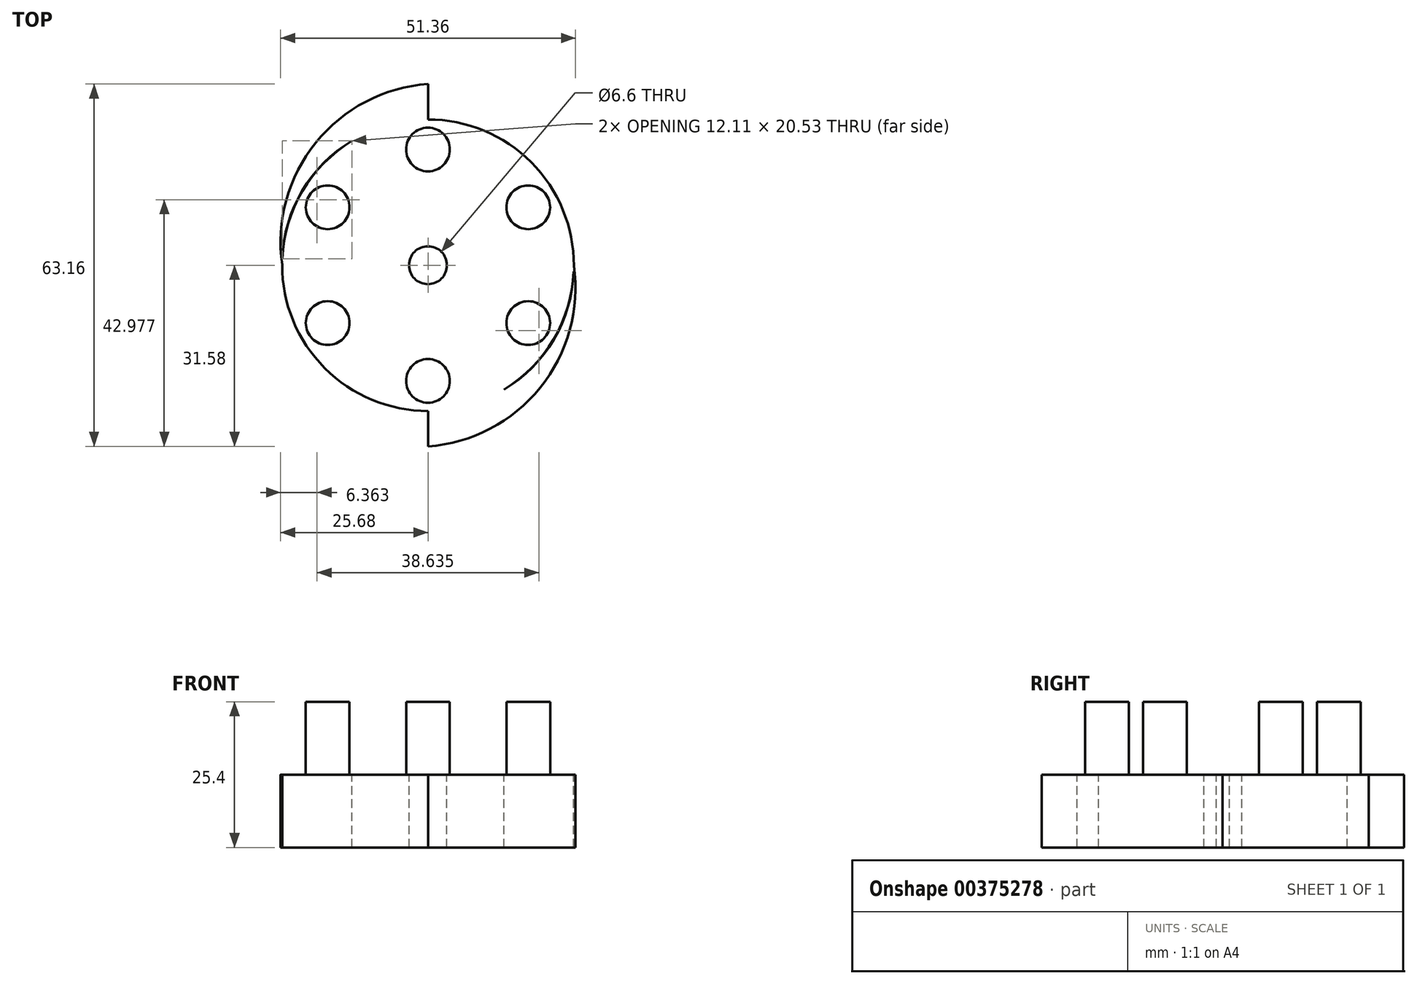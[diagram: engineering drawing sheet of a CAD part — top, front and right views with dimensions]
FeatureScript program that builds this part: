
annotation { "Feature Type Name" : "Feature", "Feature Type Description" : "" }
export const myFeature = defineFeature(function(context is Context, id is Id, definition is map)
    precondition{}
    {
        {
            var Q0;
            Q0=qCreatedBy(makeId("Top.planeOp"),FACE);
            var sketch = newSketch(context, id + "F0", { "sketchPlane" : qUnion([Q0])});
            skCircle(sketch, "E0", {"center": v(0, 0) * mm, "radius": 25.4 * mm});
            skSolve(sketch);
        }
        {
            var Q0;
            Q0 = qSketchRegion(id + "F0", true);
            extrude(context, id + "F1", {"entities" : qUnion([Q0]), "oppositeDirection" : true, "depth" : 12.7 * mm});
        }
        {
            var Q0;
            Q0=qCreatedBy(makeId("Top.planeOp"),FACE);
            var sketch = newSketch(context, id + "F2", { "sketchPlane" : qUnion([Q0])});
            skLineSegment(sketch, "E1", {"start": v(0, 25.2) * mm, "end": v(0, 31.58) * mm});
            skArc(sketch, "E2", {"start": v(0, 31.58) * mm, "mid": v(-19.57, 21.32) * mm, "end": v(-25.39, 0) * mm});
            skArc(sketch, "E3", {"start": v(0, 25.2) * mm, "mid": v(-18.02, 17.97) * mm, "end": v(-25.39, 0) * mm});
            skArc(sketch, "E4.1.0", {"start": v(0, -31.58) * mm, "mid": v(19.57, -21.32) * mm, "end": v(25.39, 0) * mm});
            skArc(sketch, "E4.1.1", {"start": v(0, -25.2) * mm, "mid": v(18.02, -17.97) * mm, "end": v(25.39, 0) * mm});
            skLineSegment(sketch, "E4.1.2", {"start": v(0, -25.2) * mm, "end": v(0, -31.58) * mm});
            skPoint(sketch, "E4.center", {"position": v(0, 0) * mm});
            skSolve(sketch);
        }
        {
            var Q0;
            Q0 = qSketchRegion(id + "F2", true);
            extrude(context, id + "F3", {"entities" : qUnion([Q0]), "operationType" : NewBodyOperationType.ADD, "oppositeDirection" : true, "depth" : 12.7 * mm});
        }
        {
            var Q0;
            Q0=qCreatedBy(makeId("Top.planeOp"),FACE);
            var sketch = newSketch(context, id + "F4", { "sketchPlane" : qUnion([Q0])});
            skCircle(sketch, "E5", {"center": v(0, 20.17) * mm, "radius": 3.81 * mm});
            skCircle(sketch, "E6.1.0", {"center": v(-17.47, 10.08) * mm, "radius": 3.81 * mm});
            skCircle(sketch, "E6.2.0", {"center": v(-17.47, -10.08) * mm, "radius": 3.81 * mm});
            skCircle(sketch, "E6.3.0", {"center": v(0, -20.17) * mm, "radius": 3.81 * mm});
            skCircle(sketch, "E6.4.0", {"center": v(17.47, -10.08) * mm, "radius": 3.81 * mm});
            skCircle(sketch, "E6.5.0", {"center": v(17.47, 10.08) * mm, "radius": 3.81 * mm});
            skPoint(sketch, "E6.center", {"position": v(0, 0) * mm});
            skSolve(sketch);
        }
        {
            var Q0;
            Q0=makeQuery(id+"F4.imprint","IMPRINT",FACE,{"disambiguationData":[TD([[makeQuery(id+"F4.imprint","IMPRINT",EDGE,{"derivedFrom":sQuery(id+"F4.wireOp",EDGE,"E6.1.0")}),1.0]])]});
            var Q1;
            Q1=makeQuery(id+"F4.imprint","IMPRINT",FACE,{"disambiguationData":[TD([[makeQuery(id+"F4.imprint","IMPRINT",EDGE,{"derivedFrom":sQuery(id+"F4.wireOp",EDGE,"E5")}),1.0]])]});
            var Q2;
            Q2=makeQuery(id+"F4.imprint","IMPRINT",FACE,{"disambiguationData":[TD([[makeQuery(id+"F4.imprint","IMPRINT",EDGE,{"derivedFrom":sQuery(id+"F4.wireOp",EDGE,"E6.5.0")}),1.0]])]});
            var Q3;
            Q3=makeQuery(id+"F4.imprint","IMPRINT",FACE,{"disambiguationData":[TD([[makeQuery(id+"F4.imprint","IMPRINT",EDGE,{"derivedFrom":sQuery(id+"F4.wireOp",EDGE,"E6.4.0")}),1.0]])]});
            var Q4;
            Q4=makeQuery(id+"F4.imprint","IMPRINT",FACE,{"disambiguationData":[TD([[makeQuery(id+"F4.imprint","IMPRINT",EDGE,{"derivedFrom":sQuery(id+"F4.wireOp",EDGE,"E6.3.0")}),1.0]])]});
            var Q5;
            Q5=makeQuery(id+"F4.imprint","IMPRINT",FACE,{"disambiguationData":[TD([[makeQuery(id+"F4.imprint","IMPRINT",EDGE,{"derivedFrom":sQuery(id+"F4.wireOp",EDGE,"E6.2.0")}),1.0]])]});
            var Q6;
            Q6=sQuery(id+"F4.wireOp",EDGE,"E6.1.0");
            var Q7;
            Q7=sQuery(id+"F4.wireOp",EDGE,"E5");
            var Q8;
            Q8=sQuery(id+"F4.wireOp",EDGE,"E6.5.0");
            var Q9;
            Q9=sQuery(id+"F4.wireOp",EDGE,"E6.4.0");
            var Q10;
            Q10=sQuery(id+"F4.wireOp",EDGE,"E6.3.0");
            var Q11;
            Q11=sQuery(id+"F4.wireOp",EDGE,"E6.2.0");
            extrude(context, id + "F5", {"entities" : qUnion([Q0, Q1, Q2, Q3, Q4, Q5]), "operationType" : NewBodyOperationType.ADD, "surfaceEntities" : qUnion([Q6, Q7, Q8, Q9, Q10, Q11]), "depth" : 12.7 * mm});
        }
        {
            var Q0;
            Q0=qCreatedBy(makeId("Top.planeOp"),FACE);
            var sketch = newSketch(context, id + "F6", { "sketchPlane" : qUnion([Q0])});
            skCircle(sketch, "E7", {"center": v(0, 0) * mm, "radius": 3.3 * mm});
            skSolve(sketch);
        }
        {
            var Q0;
            Q0 = qSketchRegion(id + "F6", true);
            extrude(context, id + "F7", {"entities" : qUnion([Q0]), "operationType" : NewBodyOperationType.REMOVE, "oppositeDirection" : true, "depth" : 12.7 * mm});
        }
    });
